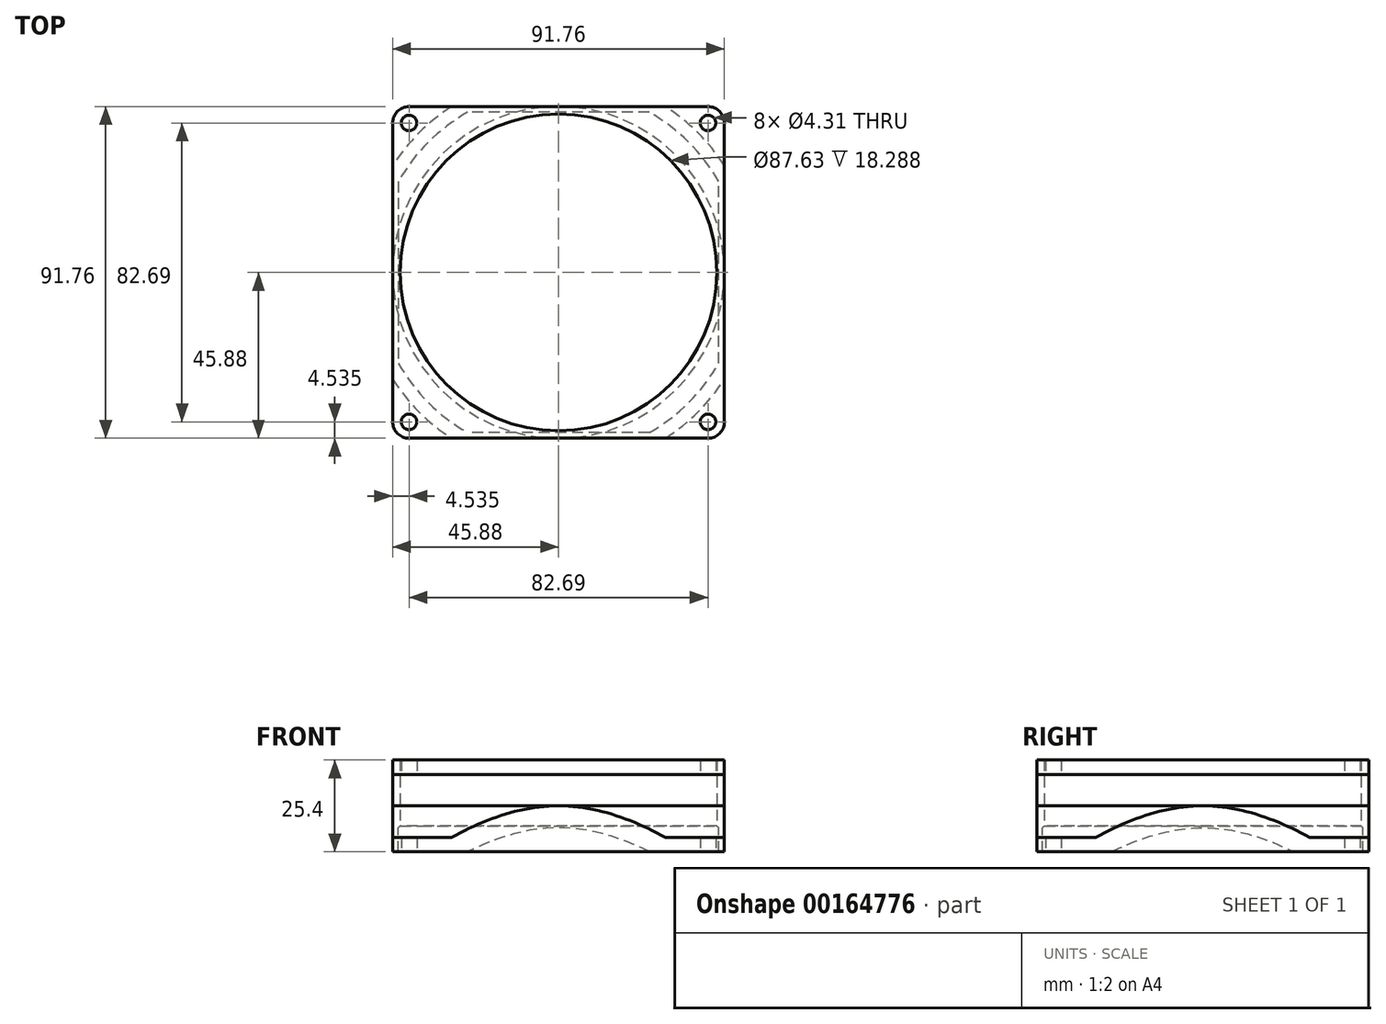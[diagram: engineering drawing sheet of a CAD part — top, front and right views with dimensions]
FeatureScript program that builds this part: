
annotation { "Feature Type Name" : "Feature", "Feature Type Description" : "" }
export const myFeature = defineFeature(function(context is Context, id is Id, definition is map)
    precondition{}
    {
        {
            var Q0;
            Q0=qCreatedBy(makeId("Top.planeOp"),FACE);
            var sketch = newSketch(context, id + "F0", { "sketchPlane" : qUnion([Q0])});
            skLineSegment(sketch, "E0.bottom", {"start": v(45.88, 45.88) * mm, "end": v(-45.88, 45.88) * mm});
            skLineSegment(sketch, "E0.top", {"start": v(45.88, -45.88) * mm, "end": v(-45.88, -45.88) * mm});
            skLineSegment(sketch, "E0.left", {"start": v(45.88, 45.88) * mm, "end": v(45.88, -45.88) * mm});
            skLineSegment(sketch, "E0.right", {"start": v(-45.88, 45.88) * mm, "end": v(-45.88, -45.88) * mm});
            skPoint(sketch, "E0.middle", {"position": v(0, 0) * mm});
            skCircle(sketch, "E1", {"center": v(0, 0) * mm, "radius": 43.82 * mm});
            skLineSegment(sketch, "E2", {"start": v(41.34, 45.88) * mm, "end": v(41.34, 41.34) * mm, "construction": true});
            skLineSegment(sketch, "E3", {"start": v(41.34, 41.34) * mm, "end": v(45.88, 41.34) * mm, "construction": true});
            skLineSegment(sketch, "E4.bottom", {"start": v(41.34, 41.34) * mm, "end": v(-41.34, 41.34) * mm, "construction": true});
            skLineSegment(sketch, "E4.top", {"start": v(41.34, -41.34) * mm, "end": v(-41.34, -41.34) * mm, "construction": true});
            skLineSegment(sketch, "E4.left", {"start": v(41.34, 41.34) * mm, "end": v(41.34, -41.34) * mm, "construction": true});
            skLineSegment(sketch, "E4.right", {"start": v(-41.34, 41.34) * mm, "end": v(-41.34, -41.34) * mm, "construction": true});
            skCircle(sketch, "E5", {"center": v(41.34, 41.34) * mm, "radius": 2.15 * mm});
            skCircle(sketch, "E6", {"center": v(-41.34, 41.34) * mm, "radius": 2.15 * mm});
            skCircle(sketch, "E7", {"center": v(-41.34, -41.34) * mm, "radius": 2.15 * mm});
            skCircle(sketch, "E8", {"center": v(41.34, -41.34) * mm, "radius": 2.15 * mm});
            skSolve(sketch);
        }
        {
            var Q0;
            Q0 = qSketchRegion(id + "F0", true);
            extrude(context, id + "F1", {"entities" : qUnion([Q0]), "depth" : 25.4 * mm});
        }
        {
            var Q0;
            Q0=makeQuery(id+"F1.opExtrude","SWEPT_EDGE",EDGE,{"disambiguationData":[OSD([sQuery(id+"F0.wireOp",EDGE,"E0.bottom"),sQuery(id+"F0.wireOp",EDGE,"E0.left")])]});
            var Q1;
            Q1=makeQuery(id+"F1.opExtrude","SWEPT_EDGE",EDGE,{"disambiguationData":[OSD([sQuery(id+"F0.wireOp",EDGE,"E0.top"),sQuery(id+"F0.wireOp",EDGE,"E0.right")])]});
            var Q2;
            Q2=makeQuery(id+"F1.opExtrude","SWEPT_EDGE",EDGE,{"disambiguationData":[OSD([sQuery(id+"F0.wireOp",EDGE,"E0.top"),sQuery(id+"F0.wireOp",EDGE,"E0.left")])]});
            var Q3;
            Q3=makeQuery(id+"F1.opExtrude","SWEPT_EDGE",EDGE,{"disambiguationData":[OSD([sQuery(id+"F0.wireOp",EDGE,"E0.bottom"),sQuery(id+"F0.wireOp",EDGE,"E0.right")])]});
            fillet(context, id + "F2", {"entities" : qUnion([Q0, Q1, Q2, Q3]), "radius" : 4.53 * mm, "tangentPropagation" : true, "allowEdgeOverflow" : false});
        }
        {
            var Q0;
            Q0=qCreatedBy(makeId("Right.planeOp"),FACE);
            var sketch = newSketch(context, id + "F3", { "sketchPlane" : qUnion([Q0])});
            skLineSegment(sketch, "E9.bottom", {"start": v(45.88, 21.4) * mm, "end": v(71.28, 21.4) * mm});
            skLineSegment(sketch, "E9.top", {"start": v(45.88, 4) * mm, "end": v(71.28, 4) * mm});
            skLineSegment(sketch, "E9.left", {"start": v(45.88, 21.4) * mm, "end": v(45.88, 4) * mm});
            skLineSegment(sketch, "E9.right", {"start": v(71.28, 21.4) * mm, "end": v(71.28, 4) * mm});
            skLineSegment(sketch, "E10", {"start": v(45.88, 21.4) * mm, "end": v(45.88, 25.4) * mm, "construction": true});
            skLineSegment(sketch, "E11", {"start": v(45.88, 4) * mm, "end": v(45.88, 0) * mm, "construction": true});
            skSolve(sketch);
        }
        {
            var Q0;
            Q0 = qSketchRegion(id + "F3", true);
            var Q1;
            Q1=makeQuery(id+"F1.opExtrude","SWEPT_FACE",FACE,{"disambiguationData":[OSD([sQuery(id+"F0.wireOp",EDGE,"E1")])]});
            revolve(context, id + "F4", {"operationType" : NewBodyOperationType.REMOVE, "entities" : qUnion([Q0]), "axis" : qUnion([Q1]), "revolveType" : RevolveType.FULL, "oppositeDirection" : true});
        }
        {
            var Q0;
            {var subQ0=sQuery(id+"F3.wireOp",EDGE,"E9.top");var subQ1=sQuery(id+"F3.wireOp",EDGE,"E9.left");Q0=makeQuery(id+"F4.boolean.opBoolean","COPY",EDGE,{"disambiguationData":[TD([makeQuery(id+"F1.opExtrude","SWEPT_FACE",FACE,{"disambiguationData":[OSD([sQuery(id+"F0.wireOp",EDGE,"E0.bottom")])]}),makeQuery(id+"F1.opExtrude","SWEPT_FACE",FACE,{"disambiguationData":[OSD([sQuery(id+"F0.wireOp",EDGE,"E0.left")])]}),makeQuery(id+"F4.opRevolve","SWEPT_FACE",FACE,{"disambiguationData":[OSD([subQ0])]}),makeQuery(id+"F4.opRevolve","SWEPT_FACE",FACE,{"disambiguationData":[OSD([subQ1])]})])],"derivedFrom":makeQuery(id+"F4.opRevolve","SWEPT_EDGE",EDGE,{"disambiguationData":[OSD([subQ0,subQ1])]})});}
            chamfer(context, id + "F5", {"entities" : qUnion([Q0]), "width" : 8.7 * mm, "tangentPropagation" : true});
        }
        {
            var Q0;
            Q0=makeQuery(id+"F1.opExtrude","CAP_EDGE",EDGE,{"disambiguationData":[OSD([sQuery(id+"F0.wireOp",EDGE,"E1")])],"isStart":true});
            chamfer(context, id + "F6", {"entities" : qUnion([Q0]), "width" : 7.11 * mm, "tangentPropagation" : true});
        }
        {
            var Q0;
            Q0=makeQuery(id+"F6.opChamfer","SPLIT",FACE,{"disambiguationData":[OD(0.0)],"derivedFrom":makeQuery(id+"F1.opExtrude","CAP_FACE",FACE,{"disambiguationData":[OSD([sQuery(id+"F0.wireOp",EDGE,"E0.bottom"),sQuery(id+"F0.wireOp",EDGE,"E0.top"),sQuery(id+"F0.wireOp",EDGE,"E0.left"),sQuery(id+"F0.wireOp",EDGE,"E0.right"),sQuery(id+"F0.wireOp",EDGE,"E1"),sQuery(id+"F0.wireOp",EDGE,"E5"),sQuery(id+"F0.wireOp",EDGE,"E6"),sQuery(id+"F0.wireOp",EDGE,"E7"),sQuery(id+"F0.wireOp",EDGE,"E8")])],"isStart":true})});
            var sketch = newSketch(context, id + "F7", { "sketchPlane" : qUnion([Q0])});
            skLineSegment(sketch, "E12.bottom", {"start": v(25.14, -45.88) * mm, "end": v(-25.14, -45.88) * mm});
            skLineSegment(sketch, "E12.top", {"start": v(25.14, -44.3) * mm, "end": v(-25.14, -44.3) * mm});
            skLineSegment(sketch, "E12.left", {"start": v(25.14, -45.88) * mm, "end": v(25.14, -44.3) * mm});
            skLineSegment(sketch, "E12.right", {"start": v(-25.14, -45.88) * mm, "end": v(-25.14, -44.3) * mm});
            skLineSegment(sketch, "E13.bottom", {"start": v(44.3, 25.14) * mm, "end": v(45.88, 25.14) * mm});
            skLineSegment(sketch, "E13.top", {"start": v(44.3, -25.14) * mm, "end": v(45.88, -25.14) * mm});
            skLineSegment(sketch, "E13.left", {"start": v(44.3, 25.14) * mm, "end": v(44.3, -25.14) * mm});
            skLineSegment(sketch, "E13.right", {"start": v(45.88, 25.14) * mm, "end": v(45.88, -25.14) * mm});
            skLineSegment(sketch, "E14.bottom", {"start": v(-44.3, -25.14) * mm, "end": v(-45.88, -25.14) * mm});
            skLineSegment(sketch, "E14.top", {"start": v(-44.3, 25.14) * mm, "end": v(-45.88, 25.14) * mm});
            skLineSegment(sketch, "E14.left", {"start": v(-44.3, -25.14) * mm, "end": v(-44.3, 25.14) * mm});
            skLineSegment(sketch, "E14.right", {"start": v(-45.88, -25.14) * mm, "end": v(-45.88, 25.14) * mm});
            skLineSegment(sketch, "E15.bottom", {"start": v(25.14, 45.88) * mm, "end": v(-25.14, 45.88) * mm});
            skLineSegment(sketch, "E15.top", {"start": v(25.14, 44.3) * mm, "end": v(-25.14, 44.3) * mm});
            skLineSegment(sketch, "E15.left", {"start": v(25.14, 45.88) * mm, "end": v(25.14, 44.3) * mm});
            skLineSegment(sketch, "E15.right", {"start": v(-25.14, 45.88) * mm, "end": v(-25.14, 44.3) * mm});
            skLineSegment(sketch, "E16", {"start": v(0, -44.3) * mm, "end": v(0, 44.3) * mm, "construction": true});
            skLineSegment(sketch, "E17", {"start": v(44.3, 0) * mm, "end": v(-44.3, 0) * mm, "construction": true});
            skSolve(sketch);
        }
        {
            var Q0;
            Q0 = qSketchRegion(id + "F7", true);
            var Q1;
            {var subQ0=sQuery(id+"F3.wireOp",EDGE,"E9.top");var subQ1=sQuery(id+"F3.wireOp",EDGE,"E9.left");Q1=makeQuery(id+"F5.opChamfer","BLEND_FACE",FACE,{"disambiguationData":[OSD([subQ0,subQ1]),TDD([makeQuery(id+"F4.boolean.opBoolean","COPY",EDGE,{"disambiguationData":[TD([makeQuery(id+"F1.opExtrude","SWEPT_FACE",FACE,{"disambiguationData":[OSD([sQuery(id+"F0.wireOp",EDGE,"E0.top")])]}),makeQuery(id+"F1.opExtrude","SWEPT_FACE",FACE,{"disambiguationData":[OSD([sQuery(id+"F0.wireOp",EDGE,"E0.left")])]}),makeQuery(id+"F4.opRevolve","SWEPT_FACE",FACE,{"disambiguationData":[OSD([subQ0])]}),makeQuery(id+"F4.opRevolve","SWEPT_FACE",FACE,{"disambiguationData":[OSD([subQ1])]})])],"derivedFrom":makeQuery(id+"F4.opRevolve","SWEPT_EDGE",EDGE,{"disambiguationData":[OSD([subQ0,subQ1])]})})])]});}
            extrude(context, id + "F8", {"entities" : qUnion([Q0]), "operationType" : NewBodyOperationType.ADD, "endBound" : BoundingType.UP_TO_SURFACE, "oppositeDirection" : true, "endBoundEntityFace" : qUnion([Q1]), "depth" : 25.4 * mm});
        }
    });
